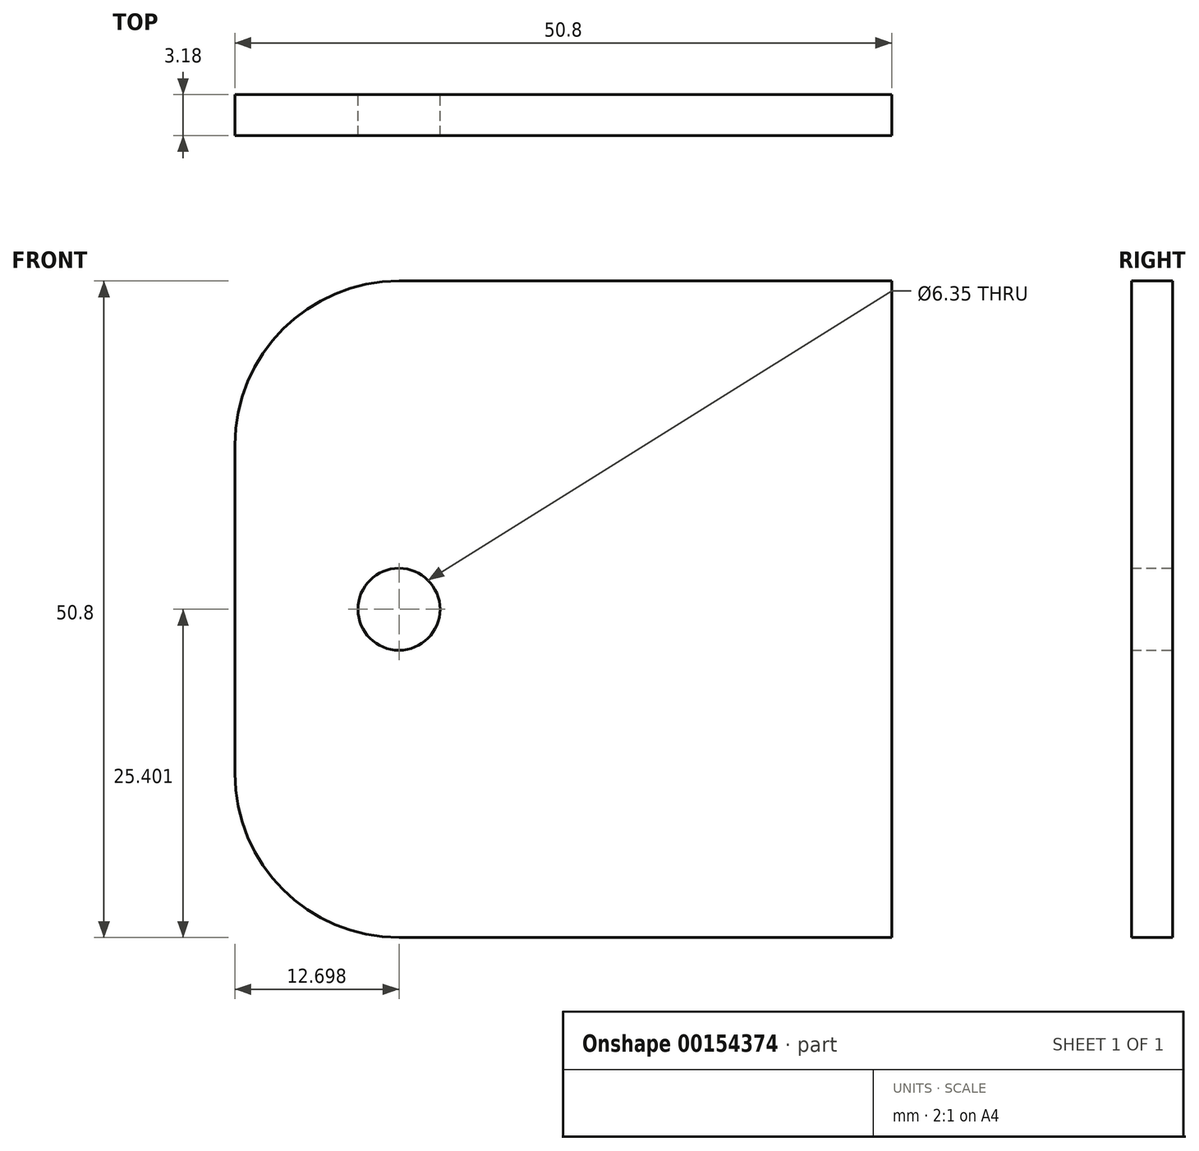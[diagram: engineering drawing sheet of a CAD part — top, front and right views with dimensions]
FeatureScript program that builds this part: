
annotation { "Feature Type Name" : "Feature", "Feature Type Description" : "" }
export const myFeature = defineFeature(function(context is Context, id is Id, definition is map)
    precondition{}
    {
        {
            var Q0;
            Q0=qCreatedBy(makeId("Front.planeOp"),FACE);
            var sketch = newSketch(context, id + "F0", { "sketchPlane" : qUnion([Q0])});
            skLineSegment(sketch, "E0.bottom", {"start": v(-17.51, 20.03) * mm, "end": v(20.59, 20.03) * mm});
            skLineSegment(sketch, "E0.top", {"start": v(-17.51, -30.77) * mm, "end": v(20.59, -30.77) * mm});
            skLineSegment(sketch, "E0.left", {"start": v(-30.21, 7.33) * mm, "end": v(-30.21, -18.07) * mm});
            skLineSegment(sketch, "E0.right", {"start": v(20.59, 20.03) * mm, "end": v(20.59, -30.77) * mm});
            skPoint(sketch, "E1.visualSharp", {"position": v(-30.21, 20.03) * mm});
            skArc(sketch, "E1.filletArc", {"start": v(-17.51, 20.03) * mm, "mid": v(-26.5, 16.31) * mm, "end": v(-30.21, 7.33) * mm});
            skPoint(sketch, "E2.visualSharp", {"position": v(-30.21, -30.77) * mm});
            skArc(sketch, "E2.filletArc", {"start": v(-30.21, -18.07) * mm, "mid": v(-26.5, -27.05) * mm, "end": v(-17.51, -30.77) * mm});
            skCircle(sketch, "E3", {"center": v(-17.51, -5.37) * mm, "radius": 3.18 * mm});
            skPoint(sketch, "E4.orphan", {"position": v(-30.21, -5.37) * mm});
            skPoint(sketch, "E5.orphan", {"position": v(20.59, -5.37) * mm});
            skSolve(sketch);
        }
        {
            var Q0;
            Q0 = qSketchRegion(id + "F0", true);
            extrude(context, id + "F1", {"entities" : qUnion([Q0]), "depth" : 3.17 * mm});
        }
    });
